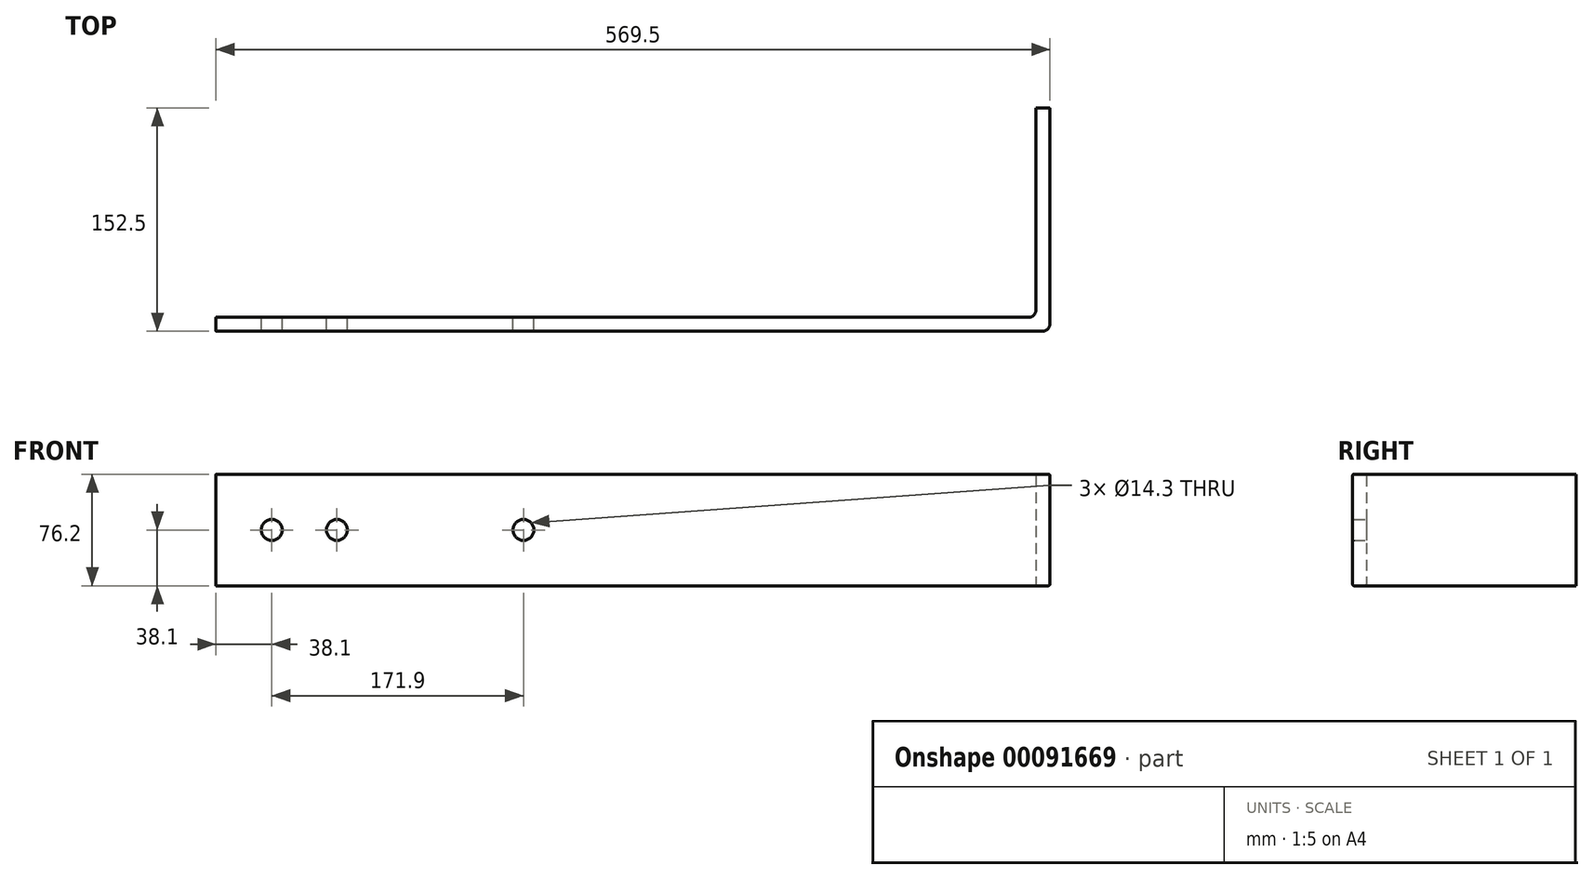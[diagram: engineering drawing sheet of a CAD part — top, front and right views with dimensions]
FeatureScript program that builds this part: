
annotation { "Feature Type Name" : "Feature", "Feature Type Description" : "" }
export const myFeature = defineFeature(function(context is Context, id is Id, definition is map)
    precondition{}
    {
        {
            var Q0;
            Q0=qCreatedBy(makeId("Top.planeOp"),FACE);
            var sketch = newSketch(context, id + "F0", { "sketchPlane" : qUnion([Q0])});
            skLineSegment(sketch, "E0", {"start": v(0, 0) * mm, "end": v(569.5, 0) * mm});
            skLineSegment(sketch, "E1", {"start": v(569.5, 0) * mm, "end": v(569.5, 152.5) * mm});
            skLineSegment(sketch, "E2", {"start": v(569.5, 152.5) * mm, "end": v(560, 152.5) * mm});
            skLineSegment(sketch, "E3", {"start": v(560, 152.5) * mm, "end": v(560, 9.5) * mm});
            skLineSegment(sketch, "E4", {"start": v(560, 9.5) * mm, "end": v(0, 9.5) * mm});
            skLineSegment(sketch, "E5", {"start": v(0, 9.5) * mm, "end": v(0, 0) * mm});
            skSolve(sketch);
        }
        {
            var Q0;
            Q0=makeQuery(id+"F0.imprint","IMPRINT",FACE,{"disambiguationData":[TD([[makeQuery(id+"F0.imprint","IMPRINT",EDGE,{"derivedFrom":sQuery(id+"F0.wireOp",EDGE,"E0")}),1.0]])]});
            extrude(context, id + "F1", {"entities" : qUnion([Q0]), "depth" : 76.2 * mm});
        }
        {
            var Q0;
            Q0=makeQuery(id+"F1.opExtrude","SWEPT_FACE",FACE,{"disambiguationData":[OSD([sQuery(id+"F0.wireOp",EDGE,"E4")])]});
            var sketch = newSketch(context, id + "F2", { "sketchPlane" : qUnion([Q0])});
            skCircle(sketch, "E6", {"center": v(-38.1, 38.1) * mm, "radius": 7.15 * mm});
            skPoint(sketch, "E6.centerSnap0", {"position": v(0, 38.1) * mm});
            skCircle(sketch, "E7", {"center": v(-82.6, 38.1) * mm, "radius": 7.15 * mm});
            skCircle(sketch, "E8", {"center": v(-210, 38.1) * mm, "radius": 7.15 * mm});
            skSolve(sketch);
        }
        {
            var Q0;
            Q0=makeQuery(id+"F2.imprint","IMPRINT",FACE,{"disambiguationData":[TD([[makeQuery(id+"F2.imprint","IMPRINT",EDGE,{"derivedFrom":sQuery(id+"F2.wireOp",EDGE,"E6")}),1.0]])]});
            var Q1;
            Q1=makeQuery(id+"F2.imprint","IMPRINT",FACE,{"disambiguationData":[TD([[makeQuery(id+"F2.imprint","IMPRINT",EDGE,{"derivedFrom":sQuery(id+"F2.wireOp",EDGE,"E7")}),1.0]])]});
            var Q2;
            Q2=makeQuery(id+"F2.imprint","IMPRINT",FACE,{"disambiguationData":[TD([[makeQuery(id+"F2.imprint","IMPRINT",EDGE,{"derivedFrom":sQuery(id+"F2.wireOp",EDGE,"E8")}),1.0]])]});
            extrude(context, id + "F3", {"entities" : qUnion([Q0, Q1, Q2]), "operationType" : NewBodyOperationType.REMOVE, "endBound" : BoundingType.THROUGH_ALL, "oppositeDirection" : true, "depth" : 25 * mm});
        }
        {
            var Q0;
            Q0=makeQuery(id+"F1.opExtrude","SWEPT_EDGE",EDGE,{"disambiguationData":[OSD([sQuery(id+"F0.wireOp",EDGE,"E0"),sQuery(id+"F0.wireOp",EDGE,"E1")])]});
            var Q1;
            Q1=makeQuery(id+"F1.opExtrude","SWEPT_EDGE",EDGE,{"disambiguationData":[OSD([sQuery(id+"F0.wireOp",EDGE,"E3"),sQuery(id+"F0.wireOp",EDGE,"E4")])]});
            fillet(context, id + "F4", {"entities" : qUnion([Q0, Q1]), "radius" : 5 * mm, "tangentPropagation" : true, "allowEdgeOverflow" : false});
        }
        {
            var Q0;
            Q0=makeQuery(id+"F1.opExtrude","CAP_EDGE",EDGE,{"disambiguationData":[OSD([sQuery(id+"F0.wireOp",EDGE,"E4")])],"isStart":false});
            var Q1;
            Q1=makeQuery(id+"F1.opExtrude","CAP_EDGE",EDGE,{"disambiguationData":[OSD([sQuery(id+"F0.wireOp",EDGE,"E4")])],"isStart":true});
            var Q2;
            Q2=makeQuery(id+"F1.opExtrude","CAP_EDGE",EDGE,{"disambiguationData":[OSD([sQuery(id+"F0.wireOp",EDGE,"E0")])],"isStart":false});
            var Q3;
            Q3=makeQuery(id+"F1.opExtrude","CAP_EDGE",EDGE,{"disambiguationData":[OSD([sQuery(id+"F0.wireOp",EDGE,"E0")])],"isStart":true});
            var Q4;
            Q4=makeQuery(id+"F1.opExtrude","CAP_EDGE",EDGE,{"disambiguationData":[OSD([sQuery(id+"F0.wireOp",EDGE,"E3")])],"isStart":true});
            var Q5;
            Q5=makeQuery(id+"F1.opExtrude","CAP_EDGE",EDGE,{"disambiguationData":[OSD([sQuery(id+"F0.wireOp",EDGE,"E1")])],"isStart":true});
            var Q6;
            Q6=makeQuery(id+"F1.opExtrude","CAP_EDGE",EDGE,{"disambiguationData":[OSD([sQuery(id+"F0.wireOp",EDGE,"E1")])],"isStart":false});
            var Q7;
            Q7=makeQuery(id+"F1.opExtrude","CAP_EDGE",EDGE,{"disambiguationData":[OSD([sQuery(id+"F0.wireOp",EDGE,"E3")])],"isStart":false});
            fillet(context, id + "F5", {"entities" : qUnion([Q0, Q1, Q2, Q3, Q4, Q5, Q6, Q7]), "radius" : 1 * mm, "tangentPropagation" : true, "allowEdgeOverflow" : false});
        }
        {
            var Q0;
            Q0=makeQuery(id+"F3.boolean.opBoolean","INTERSECT",EDGE,{"derivedFrom":[makeQuery(id+"F1.opExtrude","SWEPT_FACE",FACE,{"disambiguationData":[OSD([sQuery(id+"F0.wireOp",EDGE,"E0")])]}),makeQuery(id+"F3.opExtrude","SWEPT_FACE",FACE,{"disambiguationData":[OSD([sQuery(id+"F2.wireOp",EDGE,"E8")])]})]});
            var Q1;
            Q1=makeQuery(id+"F3.boolean.opBoolean","INTERSECT",EDGE,{"derivedFrom":[makeQuery(id+"F1.opExtrude","SWEPT_FACE",FACE,{"disambiguationData":[OSD([sQuery(id+"F0.wireOp",EDGE,"E0")])]}),makeQuery(id+"F3.opExtrude","SWEPT_FACE",FACE,{"disambiguationData":[OSD([sQuery(id+"F2.wireOp",EDGE,"E7")])]})]});
            var Q2;
            Q2=makeQuery(id+"F3.boolean.opBoolean","INTERSECT",EDGE,{"derivedFrom":[makeQuery(id+"F1.opExtrude","SWEPT_FACE",FACE,{"disambiguationData":[OSD([sQuery(id+"F0.wireOp",EDGE,"E0")])]}),makeQuery(id+"F3.opExtrude","SWEPT_FACE",FACE,{"disambiguationData":[OSD([sQuery(id+"F2.wireOp",EDGE,"E6")])]})]});
            var Q3;
            Q3=makeQuery(id+"F3.boolean.opBoolean","COPY",EDGE,{"derivedFrom":makeQuery(id+"F3.opExtrude","CAP_EDGE",EDGE,{"disambiguationData":[OSD([sQuery(id+"F2.wireOp",EDGE,"E8")])],"isStart":true})});
            var Q4;
            Q4=makeQuery(id+"F3.boolean.opBoolean","COPY",EDGE,{"derivedFrom":makeQuery(id+"F3.opExtrude","CAP_EDGE",EDGE,{"disambiguationData":[OSD([sQuery(id+"F2.wireOp",EDGE,"E7")])],"isStart":true})});
            var Q5;
            Q5=makeQuery(id+"F3.boolean.opBoolean","COPY",EDGE,{"derivedFrom":makeQuery(id+"F3.opExtrude","CAP_EDGE",EDGE,{"disambiguationData":[OSD([sQuery(id+"F2.wireOp",EDGE,"E6")])],"isStart":true})});
            fillet(context, id + "F6", {"entities" : qUnion([Q0, Q1, Q2, Q3, Q4, Q5]), "radius" : 1 * mm, "tangentPropagation" : true, "allowEdgeOverflow" : false});
        }
    });
